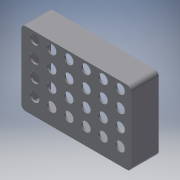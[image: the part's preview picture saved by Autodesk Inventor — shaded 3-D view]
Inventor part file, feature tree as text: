
AUTODESK INVENTOR PART (.ipt)
format: ipt  version: 2019.4 (Build 234330000, 330)  size: 257,536 bytes
history: native  units: mm
features: reference x9, extrude x3, sketch x3, other x3, fillet x1, projected_geometry x1
ambient origin geometry x8: Origin, YZ Plane, XZ Plane, XY Plane, X Axis, Y Axis, Z Axis, Center Point
bodies: Solid1 (feature_tree)
feature tree (20):
  extrude  "Extrusion1"  Depth=5.0mm
  fillet  "Fillet1"  Radius=11.0mm
  extrude  "Extrusion2"  Depth=2.0mm
  extrude  "Extrusion3"  Depth=30.0mm
  sketch  "Sketch1"  dims[d0=2.0mm d1=0.0mm d2=5.0mm d10=11.0mm]
  reference  "Reference1"
  reference  "Reference2"
  reference  "Reference3"
  reference  "Reference4"
  reference  "Reference5"
  sketch  "Sketch2"  dims[d13=2.0mm d14=0.0mm d15=40.0mm d17=19.28mm d18=60.0mm d20=19.89mm]
  other  "Image1"
  reference  "Reference6"
  reference  "Reference7"
  reference  "Reference8"
  reference  "Reference9"
  sketch  "Sketch3"  dims[d24=18.21mm d25=10.07mm d26=132.527151mm d27=2.5mm d28=30.0mm d29=0.0mm]
  projected_geometry  "Projected Loop1"
  other  "Assembly1"
  other  "00_MTP_96-welplate:1"
